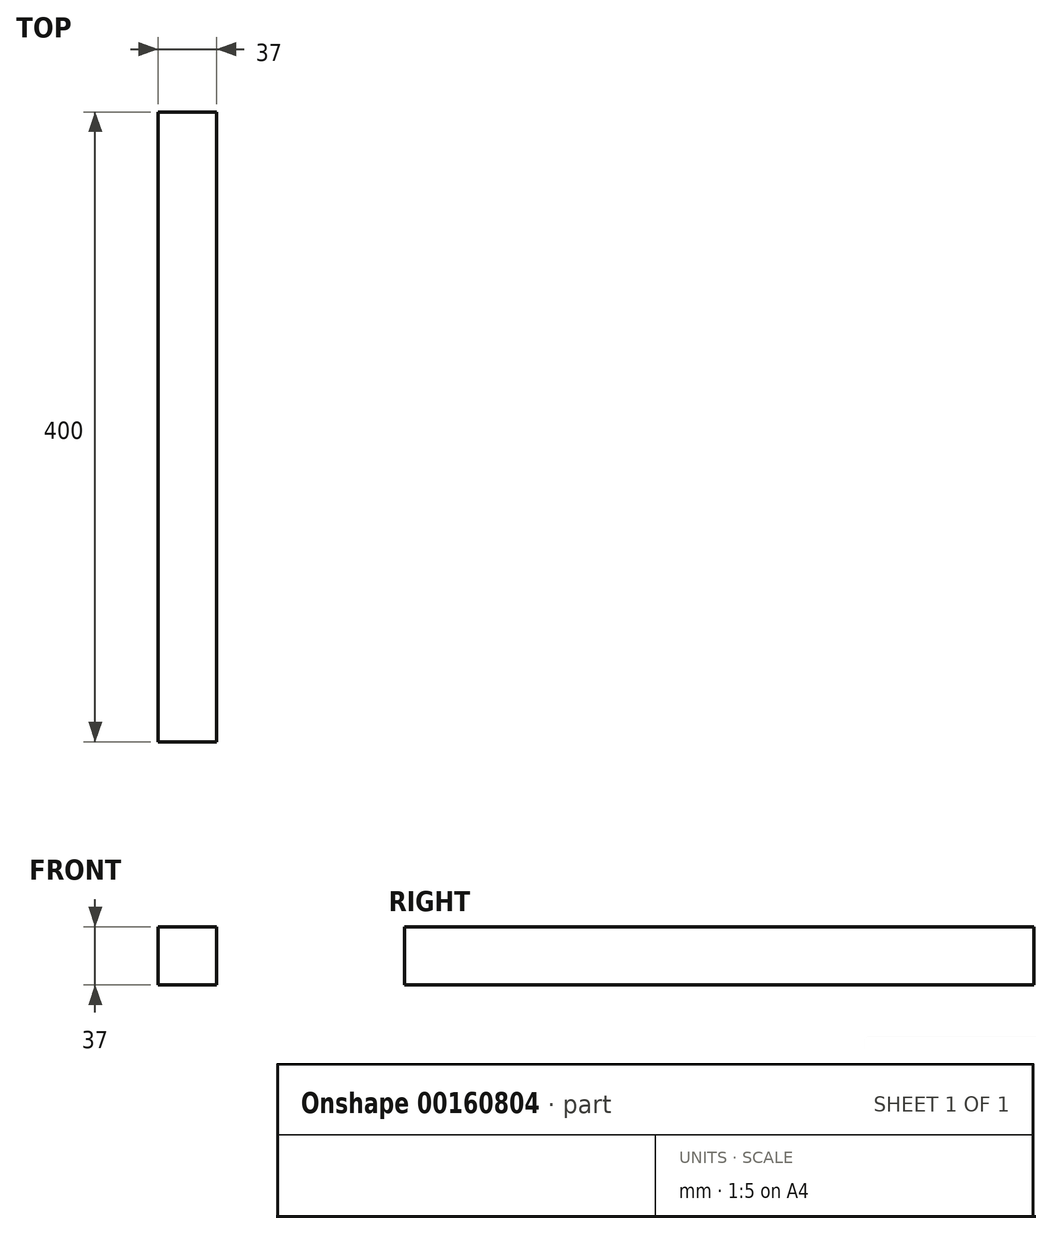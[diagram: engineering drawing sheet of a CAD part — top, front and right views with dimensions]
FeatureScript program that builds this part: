
annotation { "Feature Type Name" : "Feature", "Feature Type Description" : "" }
export const myFeature = defineFeature(function(context is Context, id is Id, definition is map)
    precondition{}
    {
        {
            var Q0;
            Q0=qCreatedBy(makeId("Front.planeOp"),FACE);
            var sketch = newSketch(context, id + "F0", { "sketchPlane" : qUnion([Q0])});
            skLineSegment(sketch, "E0.bottom", {"start": v(-76.16, 46.96) * mm, "end": v(-39.16, 46.96) * mm});
            skLineSegment(sketch, "E0.top", {"start": v(-76.16, 9.96) * mm, "end": v(-39.16, 9.96) * mm});
            skLineSegment(sketch, "E0.left", {"start": v(-76.16, 46.96) * mm, "end": v(-76.16, 9.96) * mm});
            skLineSegment(sketch, "E0.right", {"start": v(-39.16, 46.96) * mm, "end": v(-39.16, 9.96) * mm});
            skSolve(sketch);
        }
        {
            var Q0;
            Q0=makeQuery(id+"F0.imprint","IMPRINT",FACE,{"disambiguationData":[TD([[makeQuery(id+"F0.imprint","IMPRINT",EDGE,{"derivedFrom":sQuery(id+"F0.wireOp",EDGE,"E0.bottom")}),-1.0]])]});
            extrude(context, id + "F1", {"entities" : qUnion([Q0]), "depth" : 400 * mm});
        }
    });
